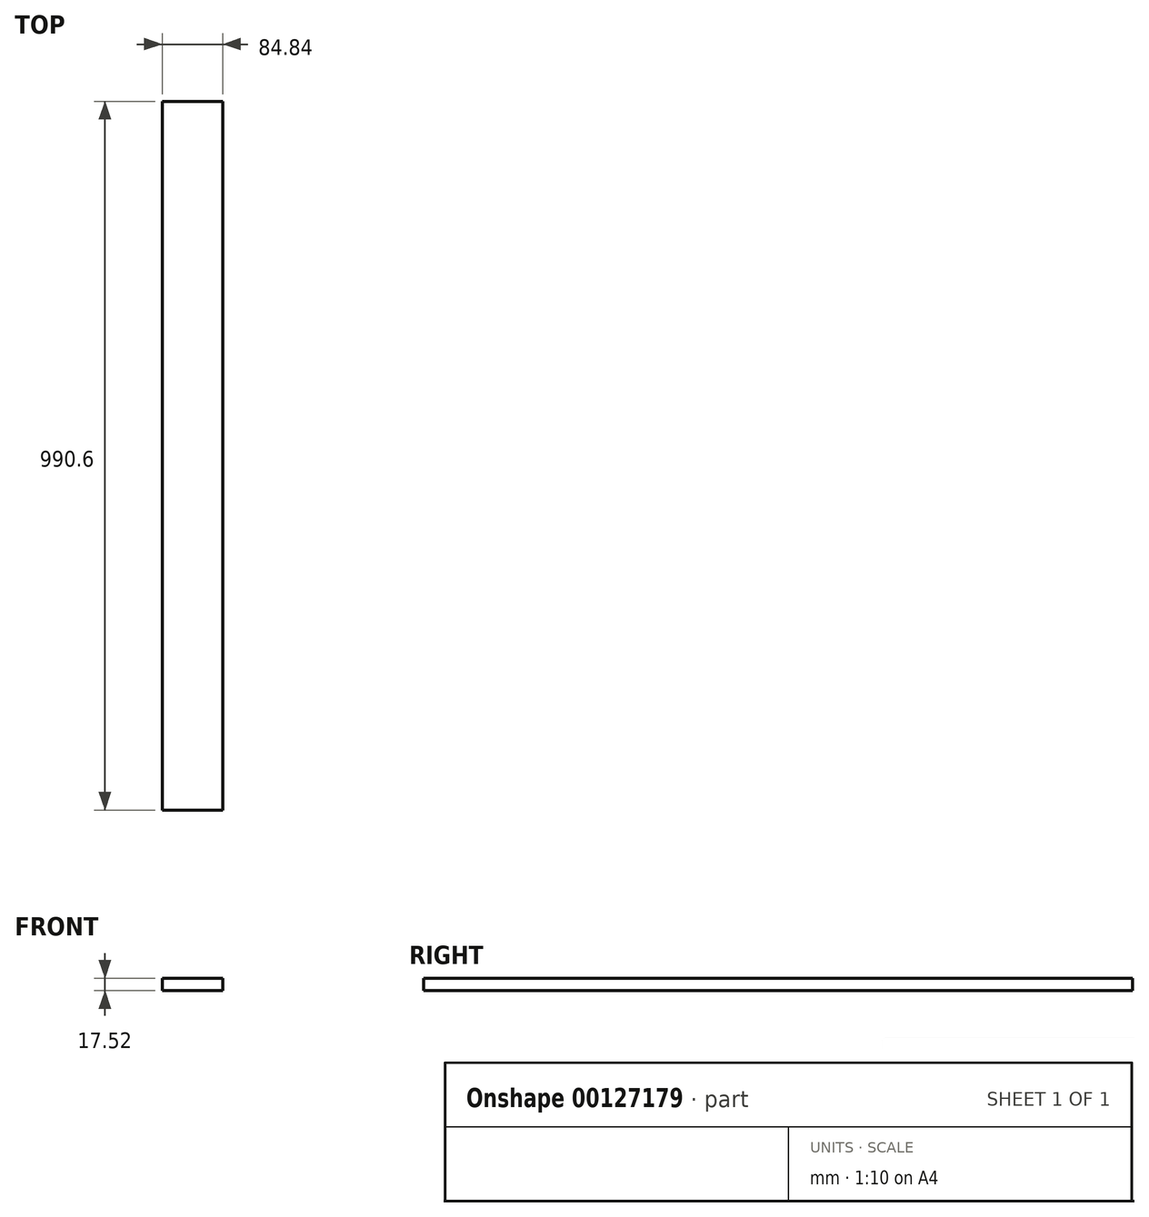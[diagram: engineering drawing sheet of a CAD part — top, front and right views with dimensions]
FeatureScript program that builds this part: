
annotation { "Feature Type Name" : "Feature", "Feature Type Description" : "" }
export const myFeature = defineFeature(function(context is Context, id is Id, definition is map)
    precondition{}
    {
        {
            var Q0;
            Q0=qCreatedBy(makeId("Front.planeOp"),FACE);
            var sketch = newSketch(context, id + "F0", { "sketchPlane" : qUnion([Q0])});
            skLineSegment(sketch, "E0.bottom", {"start": v(42.42, -8.76) * mm, "end": v(-42.42, -8.76) * mm});
            skLineSegment(sketch, "E0.top", {"start": v(42.42, 8.76) * mm, "end": v(-42.42, 8.76) * mm});
            skLineSegment(sketch, "E0.left", {"start": v(42.42, -8.76) * mm, "end": v(42.42, 8.76) * mm});
            skLineSegment(sketch, "E0.right", {"start": v(-42.42, -8.76) * mm, "end": v(-42.42, 8.76) * mm});
            skPoint(sketch, "E0.middle", {"position": v(0, 0) * mm});
            skSolve(sketch);
        }
        {
            var Q0;
            Q0=qSketchRegion(id+"F0",true);
            extrude(context, id + "F1", {"entities" : qUnion([Q0]), "depth" : 990.6 * mm, "offsetDistance" : 25.4 * mm});
        }
    });
